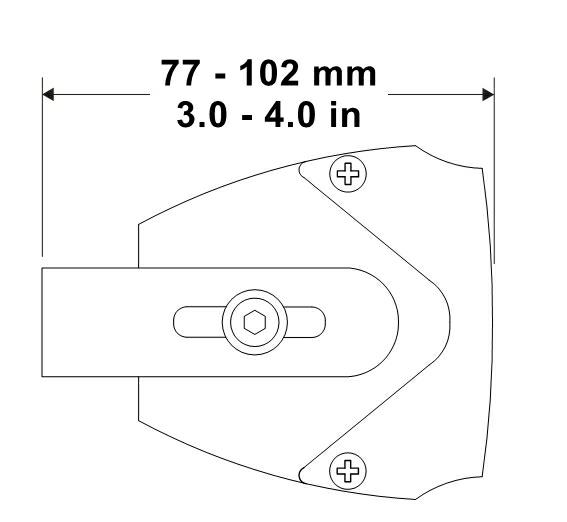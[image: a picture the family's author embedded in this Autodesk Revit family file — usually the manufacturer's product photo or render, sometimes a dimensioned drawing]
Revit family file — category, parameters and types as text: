
# Revit family: Electronics_Desono_Biamp_Two-Way-Column-Loudspeaker_COLW81
name_source: partatom
category: Communication Devices
units: mm (PartAtom-declared; Revit-internal decimal feet)

## family parameters
Cut with Voids When Loaded = No
Host = Face
Maintain Annotation Orientation = No
OmniClass Number = 23.85.10.11.14.14.14
OmniClass Title = Loudspeakers
Part Type = Normal
Room Calculation Point = No
Round Connector Dimension = Use Diameter
Shared = No

## types (1)
- COLW81
    Bracket Material = Biamp - Metal - White
    Connector Description = Terminal block; Low impedance 8 ohms, 70V/100V operation
    Continuous Power Handling Nominal Impedance = 25V; 80W @ 8Ω (320W peak)
    Controls = None; select transformer tap or low impedance input via terminal block wiring
    Default Elevation = 4' - 0"
    Depth = 0' - 3 1/2"
    Description = Desono™ COLW81 Two-Way 8 x 3.3 Column Loudspeaker
    Environmental = IP66 per IEC 60529
    Grill Material = Biamp - Plastic - White(Grid)
    Height = 3' - 2 1/2"
    Housing Material = Biamp - Plastic - White
    Input Connection = Multi-position pass-through, screw-down terminal block
    Manufacturer = Biamp
    Model = COLW81
    Mounting Provisions = Adjustable tilt L-bracket
    Nominal Beamwidth (H x V) = 100° x 10°
    Nominal Maximum SPL @ 1m = Peak - 122dB; Continuous - 116dB
    Nominal Sensitivity @ 1m = 1W - 97dB; 2.83V - 97dB
    Operating Environment = Indoor/Outdoor
    Operating Mode = Passive
    Operating Range (-10dB) = 165 Hz to 17 kHz
    Product Documentation Link = https://downloads.biamp.com
    Product Page URL = https://www.biamp.com
    Product data url = https://www.bimobject.com
    Recommended Amplifers = 80W - 160W @ 8Ω (25V - 36V)
    Shipping Weight = 15.60 lb
    Transducers = LF 8 x 3.3 (84 mm) coated paper cone HF 1 x 1 (25 mm) soft dome
    Transformer = 70V: 80W, 40W, 20W, 15W; 100V: 80W, 40W, 30W
    URL = https://www.biamp.com
    Weight = 14.77 lb
    Width = 0' - 4"

## geometry (parser evidence)
native form markers: Sweep x5
no freeform markers — native parametric forms only
